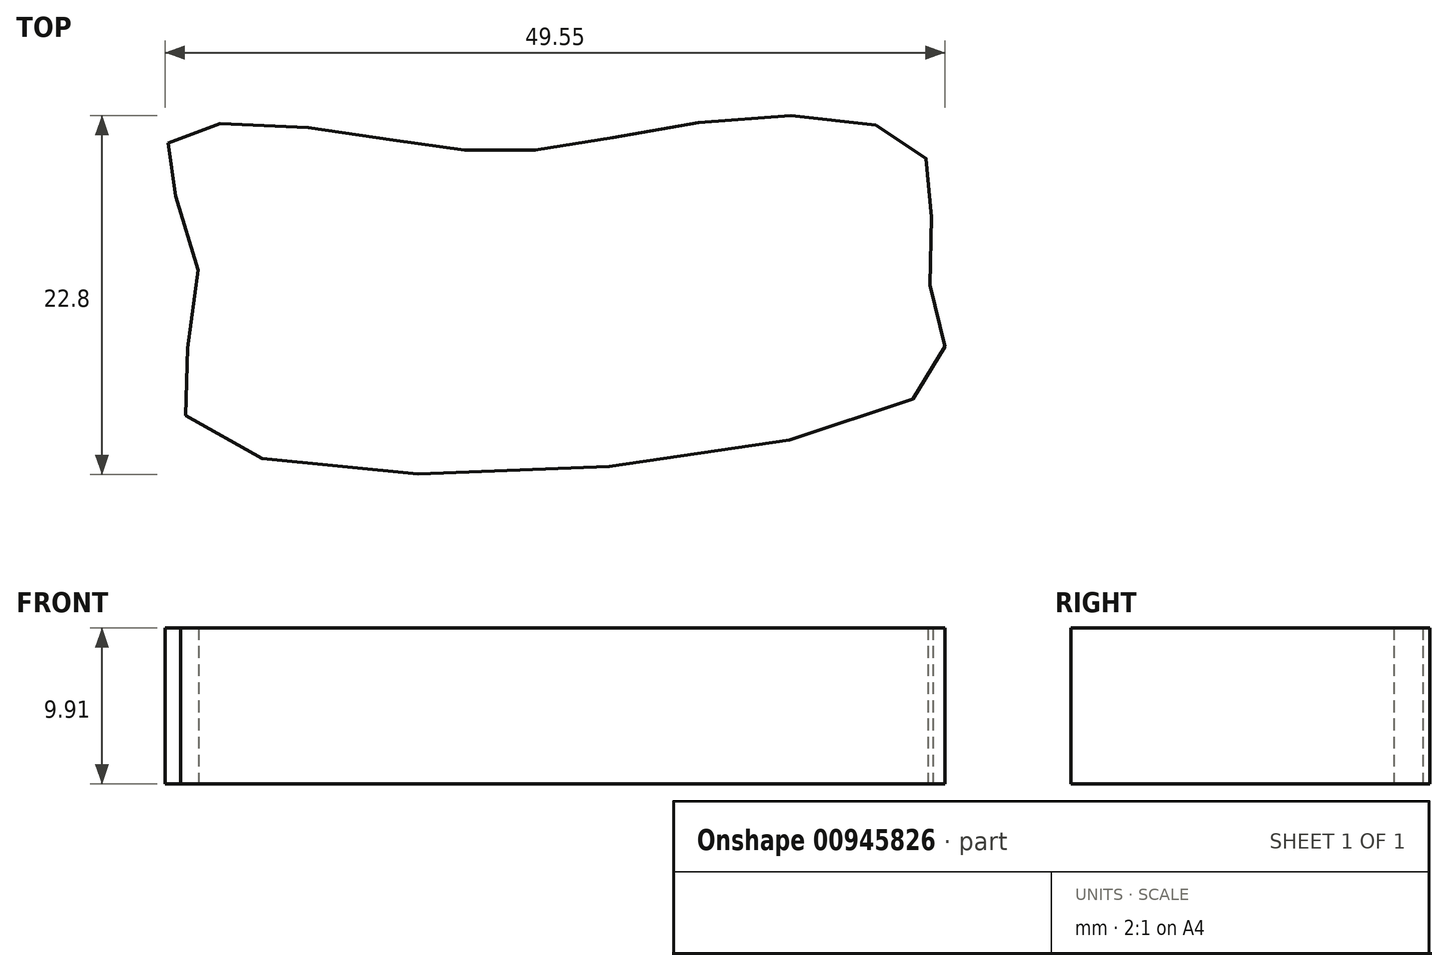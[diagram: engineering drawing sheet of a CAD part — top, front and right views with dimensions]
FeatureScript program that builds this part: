
annotation { "Feature Type Name" : "Feature", "Feature Type Description" : "" }
export const myFeature = defineFeature(function(context is Context, id is Id, definition is map)
    precondition{}
    {
        {
            var Q0;
            Q0=qCreatedBy(makeId("Top.planeOp"),FACE);
            var sketch = newSketch(context, id + "F0", { "sketchPlane" : qUnion([Q0])});
            skFitSpline(sketch, "E0", {"points": [v(-66.23, 49.16) * mm, v(-55.2, 49.87) * mm, v(-44, 48.63) * mm, v(-29.96, 50.76) * mm, v(-18.22, 48.45) * mm, v(-17.87, 40.45) * mm, v(-18.05, 33.52) * mm, v(-64.1, 30.67) * mm, v(-64.27, 40.45) * mm, v(-66.23, 49.16) * mm]});
            skSolve(sketch);
        }
        {
            var Q0;
            Q0=makeQuery(id+"F0.imprint","IMPRINT",FACE,{"disambiguationData":[TD([[makeQuery(id+"F0.imprint","IMPRINT",EDGE,{"derivedFrom":sQuery(id+"F0.wireOp",EDGE,"E0")}),-1.0]])]});
            extrude(context, id + "F1", {"entities" : qUnion([Q0]), "depth" : 9.9 * mm, "offsetDistance" : 25.4 * mm});
        }
    });
